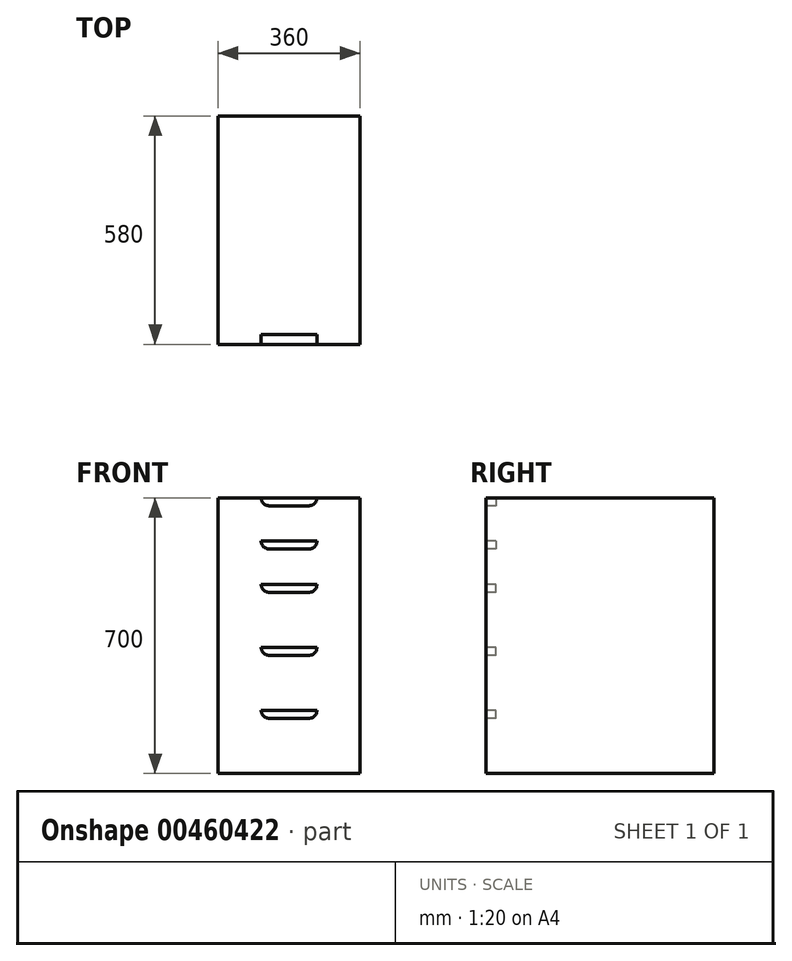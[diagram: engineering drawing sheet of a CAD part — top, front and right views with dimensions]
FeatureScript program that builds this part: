
annotation { "Feature Type Name" : "Feature", "Feature Type Description" : "" }
export const myFeature = defineFeature(function(context is Context, id is Id, definition is map)
    precondition{}
    {
        {
            var Q0;
            Q0=qCreatedBy(makeId("Top.planeOp"),FACE);
            var sketch = newSketch(context, id + "F0", { "sketchPlane" : qUnion([Q0])});
            skLineSegment(sketch, "E0.bottom", {"start": v(180, 290) * mm, "end": v(-180, 290) * mm});
            skLineSegment(sketch, "E0.top", {"start": v(180, -290) * mm, "end": v(-180, -290) * mm});
            skLineSegment(sketch, "E0.left", {"start": v(180, 290) * mm, "end": v(180, -290) * mm});
            skLineSegment(sketch, "E0.right", {"start": v(-180, 290) * mm, "end": v(-180, -290) * mm});
            skPoint(sketch, "E0.middle", {"position": v(0, 0) * mm});
            skSolve(sketch);
        }
        {
            var Q0;
            Q0=makeQuery(id+"F0.imprint","IMPRINT",FACE,{"disambiguationData":[TD([[makeQuery(id+"F0.imprint","IMPRINT",EDGE,{"derivedFrom":sQuery(id+"F0.wireOp",EDGE,"E0.bottom")}),1.0]])]});
            extrude(context, id + "F1", {"entities" : qUnion([Q0]), "depth" : 700 * mm});
        }
        {
            var Q0;
            Q0=makeQuery(id+"F1.opExtrude","SWEPT_FACE",FACE,{"disambiguationData":[OSD([sQuery(id+"F0.wireOp",EDGE,"E0.top")])]});
            var sketch = newSketch(context, id + "F2", { "sketchPlane" : qUnion([Q0])});
            skPoint(sketch, "E1.middle", {"position": v(0, 160) * mm});
            skLineSegment(sketch, "E2.0.1.0", {"start": v(50.8, 160) * mm, "end": v(-50.8, 160) * mm});
            skLineSegment(sketch, "E2.0.9.0", {"start": v(50.8, 320) * mm, "end": v(-50.8, 320) * mm});
            skLineSegment(sketch, "E2.0.17.0", {"start": v(50.8, 480) * mm, "end": v(-50.8, 480) * mm});
            skLineSegment(sketch, "E3", {"start": v(-50.8, 590) * mm, "end": v(50.8, 590) * mm});
            skArc(sketch, "E4.0.startCap", {"start": v(-50.8, 570) * mm, "mid": v(-64.94, 575.86) * mm, "end": v(-70.8, 590) * mm});
            skArc(sketch, "E4.0.endCap", {"start": v(70.8, 590) * mm, "mid": v(64.94, 575.86) * mm, "end": v(50.8, 570) * mm});
            skLineSegment(sketch, "E4.0.right", {"start": v(-50.8, 570) * mm, "end": v(50.8, 570) * mm});
            skArc(sketch, "E4.1.startCap", {"start": v(70.8, 480) * mm, "mid": v(64.94, 465.86) * mm, "end": v(50.8, 460) * mm});
            skArc(sketch, "E4.1.endCap", {"start": v(-50.8, 460) * mm, "mid": v(-64.94, 465.86) * mm, "end": v(-70.8, 480) * mm});
            skLineSegment(sketch, "E4.1.left", {"start": v(50.8, 460) * mm, "end": v(-50.8, 460) * mm});
            skArc(sketch, "E4.2.startCap", {"start": v(70.8, 320) * mm, "mid": v(64.94, 305.86) * mm, "end": v(50.8, 300) * mm});
            skArc(sketch, "E4.2.endCap", {"start": v(-50.8, 300) * mm, "mid": v(-64.94, 305.86) * mm, "end": v(-70.8, 320) * mm});
            skLineSegment(sketch, "E4.2.left", {"start": v(50.8, 300) * mm, "end": v(-50.8, 300) * mm});
            skArc(sketch, "E4.3.startCap", {"start": v(70.8, 160) * mm, "mid": v(64.94, 145.86) * mm, "end": v(50.8, 140) * mm});
            skArc(sketch, "E4.3.endCap", {"start": v(-50.8, 140) * mm, "mid": v(-64.94, 145.86) * mm, "end": v(-70.8, 160) * mm});
            skLineSegment(sketch, "E4.3.left", {"start": v(50.8, 140) * mm, "end": v(-50.8, 140) * mm});
            skLineSegment(sketch, "E5", {"start": v(50.8, 160) * mm, "end": v(180, 160) * mm});
            skLineSegment(sketch, "E6", {"start": v(-50.8, 590) * mm, "end": v(-180, 590) * mm});
            skLineSegment(sketch, "E7", {"start": v(-50.8, 480) * mm, "end": v(-180, 480) * mm});
            skLineSegment(sketch, "E8", {"start": v(-180, 320) * mm, "end": v(-50.8, 320) * mm});
            skLineSegment(sketch, "E9", {"start": v(-50.8, 160) * mm, "end": v(-180, 160) * mm});
            skLineSegment(sketch, "E10", {"start": v(180, 320) * mm, "end": v(50.8, 320) * mm});
            skLineSegment(sketch, "E11", {"start": v(50.8, 480) * mm, "end": v(180, 480) * mm});
            skLineSegment(sketch, "E12", {"start": v(180, 590) * mm, "end": v(50.8, 590) * mm});
            skLineSegment(sketch, "E13", {"start": v(-50.8, 700) * mm, "end": v(50.8, 700) * mm});
            skArc(sketch, "E14.0.startCap", {"start": v(-50.8, 680) * mm, "mid": v(-64.94, 685.86) * mm, "end": v(-70.8, 700) * mm});
            skArc(sketch, "E14.0.endCap", {"start": v(70.8, 700) * mm, "mid": v(64.94, 685.86) * mm, "end": v(50.8, 680) * mm});
            skLineSegment(sketch, "E14.0.right", {"start": v(-50.8, 680) * mm, "end": v(50.8, 680) * mm});
            skLineSegment(sketch, "E15", {"start": v(-50.8, 700) * mm, "end": v(-180, 700) * mm});
            skLineSegment(sketch, "E16", {"start": v(50.8, 700) * mm, "end": v(180, 700) * mm});
            skSolve(sketch);
        }
        {
            var Q0;
            {var subQ2=sQuery(id+"F2.wireOp",EDGE,"E13");Q0=makeQuery(id+"F2.imprint","IMPRINT",FACE,{"disambiguationData":[TD([[makeQuery(id+"F2.imprint","IMPRINT",EDGE,{"derivedFrom":subQ2}),1.0]])]});}
            var Q1;
            {var subQ2=sQuery(id+"F2.wireOp",EDGE,"E3");Q1=makeQuery(id+"F2.imprint","IMPRINT",FACE,{"disambiguationData":[TD([[makeQuery(id+"F2.imprint","IMPRINT",EDGE,{"derivedFrom":subQ2}),-1.0]])]});}
            var Q2;
            {var subQ1=sQuery(id+"F2.wireOp",EDGE,"E2.0.17.0");Q2=makeQuery(id+"F2.imprint","IMPRINT",FACE,{"disambiguationData":[TD([[makeQuery(id+"F2.imprint","IMPRINT",EDGE,{"derivedFrom":subQ1}),1.0]])]});}
            var Q3;
            {var subQ0=sQuery(id+"F2.wireOp",EDGE,"E2.0.9.0");Q3=makeQuery(id+"F2.imprint","IMPRINT",FACE,{"disambiguationData":[TD([[makeQuery(id+"F2.imprint","IMPRINT",EDGE,{"derivedFrom":subQ0}),1.0]])]});}
            var Q4;
            {var subQ3=sQuery(id+"F2.wireOp",EDGE,"E2.0.1.0");Q4=makeQuery(id+"F2.imprint","IMPRINT",FACE,{"disambiguationData":[TD([[makeQuery(id+"F2.imprint","IMPRINT",EDGE,{"derivedFrom":subQ3}),1.0]])]});}
            extrude(context, id + "F3", {"entities" : qUnion([Q0, Q1, Q2, Q3, Q4]), "operationType" : NewBodyOperationType.REMOVE, "oppositeDirection" : true, "depth" : 25.4 * mm});
        }
    });
